# Revit family: L-20105-DN
name_source: partatom
category: Aparatos sanitarios
units: mm (PartAtom-declared; Revit-internal decimal feet)

## family parameters
Activar corte en vistas = No
Compartido = No
Corte con vacíos al cargar = No
Cota de conector redondo = Usar diámetro
Mantener orientación de anotación = No
Número OmniClass = 23.45.00.00
Punto de cálculo de habitación = No
Se basa en plano de trabajo = No
Siempre vertical = Sí
Tipo de pieza = Normal
Título OmniClass = Sanitary, Laundry, and Cleaning Equipment

## types (1)
- L-20105-DN
    Alto = 1"
    Ancho = 3"
    Comentarios de tipo = Accesories
    Descripción = Toallero de barra
    Duna = Duna
    Elevación por defecto = 47"
    Fabricante = HELVEX
    Features = Taollero de barra que armoniza con la colección de la línea de accesorios Máxima HL.
Montaje oculto, no expone los tornillos de fijación.
Fácil de instalar.
    Imagen de tipo = L-20105.png
    Largo = 26"
    Modelo = L-20105-DN
    Titanio = Titanio

## geometry (parser evidence)
native form markers: Sweep x3
no freeform markers — native parametric forms only
